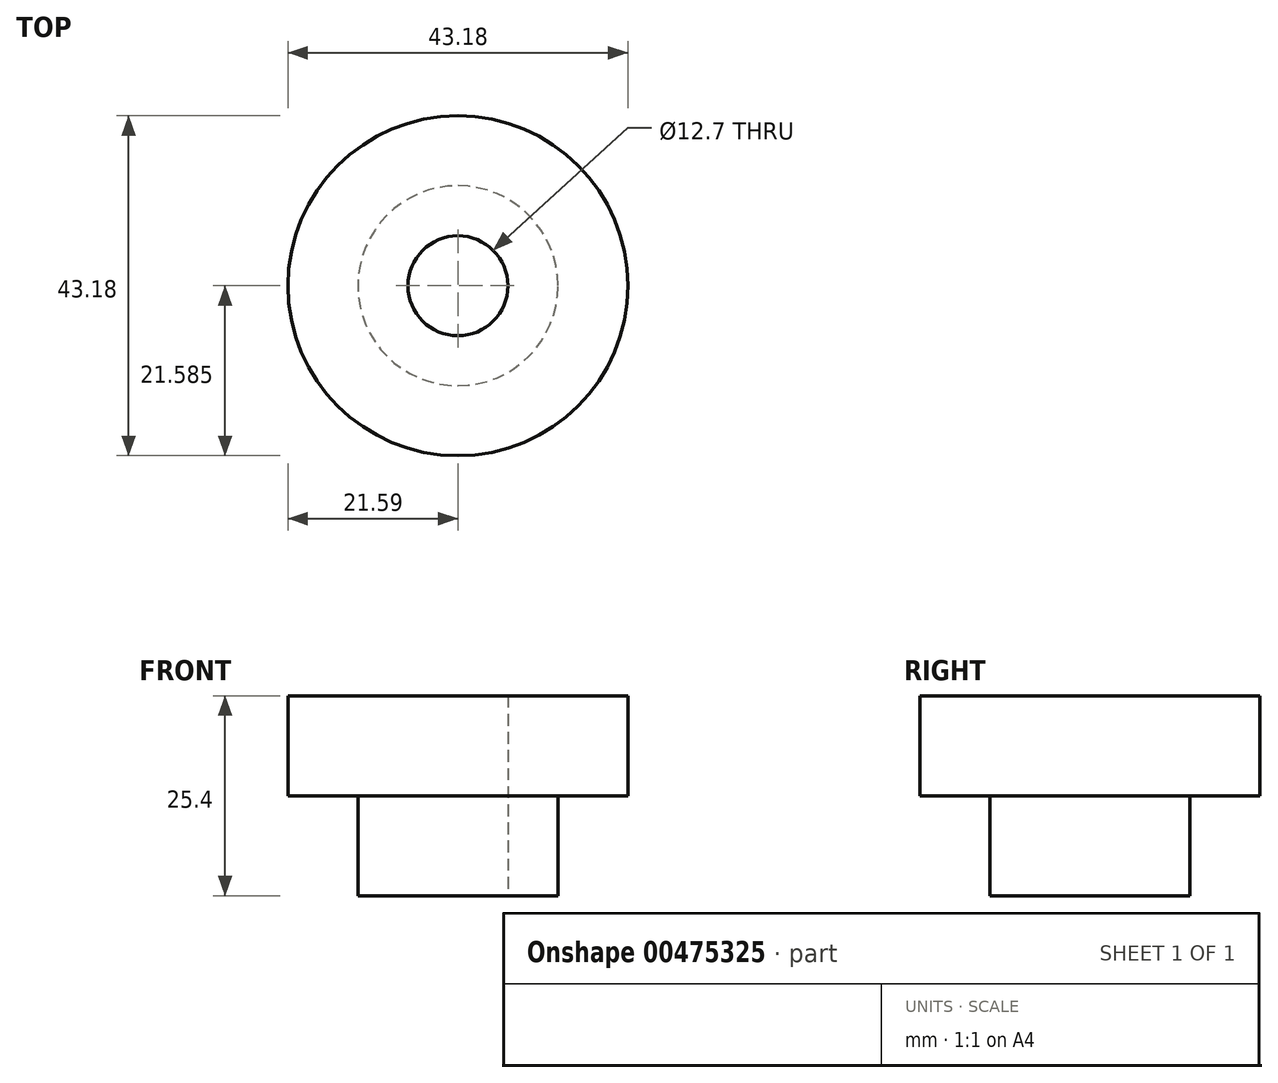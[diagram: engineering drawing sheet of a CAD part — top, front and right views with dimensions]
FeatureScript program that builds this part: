
annotation { "Feature Type Name" : "Feature", "Feature Type Description" : "" }
export const myFeature = defineFeature(function(context is Context, id is Id, definition is map)
    precondition{}
    {
        {
            var Q0;
            Q0=qCreatedBy(makeId("Top.planeOp"),FACE);
            var sketch = newSketch(context, id + "F0", { "sketchPlane" : qUnion([Q0])});
            skCircle(sketch, "E0", {"center": v(0, 39.83) * mm, "radius": 12.7 * mm});
            skCircle(sketch, "E1", {"center": v(0, -33.8) * mm, "radius": 31.75 * mm});
            skCircle(sketch, "E2", {"center": v(0, 39.83) * mm, "radius": 6.35 * mm});
            skLineSegment(sketch, "E3", {"start": v(0, 39.83) * mm, "end": v(6.35, 39.83) * mm});
            skLineSegment(sketch, "E4", {"start": v(6.35, 39.83) * mm, "end": v(12.7, 39.83) * mm});
            skSolve(sketch);
        }
        {
            var Q0;
            Q0=makeQuery(id+"F0.imprint","IMPRINT",FACE,{"disambiguationData":[TD([[makeQuery(id+"F0.imprint","IMPRINT",EDGE,{"derivedFrom":sQuery(id+"F0.wireOp",EDGE,"E0")}),1.0]])]});
            extrude(context, id + "F1", {"entities" : qUnion([Q0]), "depth" : 25.4 * mm});
        }
        {
            var Q0;
            Q0=makeQuery(id+"F1.opExtrude","CAP_FACE",FACE,{"disambiguationData":[OSD([sQuery(id+"F0.wireOp",EDGE,"E0"),sQuery(id+"F0.wireOp",EDGE,"E2")])],"isStart":false});
            var sketch = newSketch(context, id + "F2", { "sketchPlane" : qUnion([Q0])});
            skCircle(sketch, "E5", {"center": v(0, 39.83) * mm, "radius": 21.59 * mm});
            skLineSegment(sketch, "E6", {"start": v(0, 39.83) * mm, "end": v(21.59, 39.83) * mm});
            skSolve(sketch);
        }
        {
            var Q0;
            Q0=makeQuery(id+"F2.imprint","IMPRINT",FACE,{"disambiguationData":[TD([[makeQuery(id+"F2.imprint","IMPRINT",EDGE,{"derivedFrom":sQuery(id+"F2.wireOp",EDGE,"E5")}),1.0]])]});
            extrude(context, id + "F3", {"entities" : qUnion([Q0]), "operationType" : NewBodyOperationType.ADD, "oppositeDirection" : true, "depth" : 12.7 * mm});
        }
        {
            var Q0;
            Q0=makeQuery(id+"F1.opExtrude","SWEPT_BODY",BODY,{"disambiguationData":[OSD([sQuery(id+"F0.wireOp",EDGE,"E0"),sQuery(id+"F0.wireOp",EDGE,"E2")])]});
            transform(context, id + "F4", {"entities" : qUnion([Q0]), "transformType" : TransformType.TRANSLATION_3D, "dx" : 0 * mm, "dy" : -40.64 * mm, "dz" : 0 * mm, "makeCopy" : false});
        }
    });
